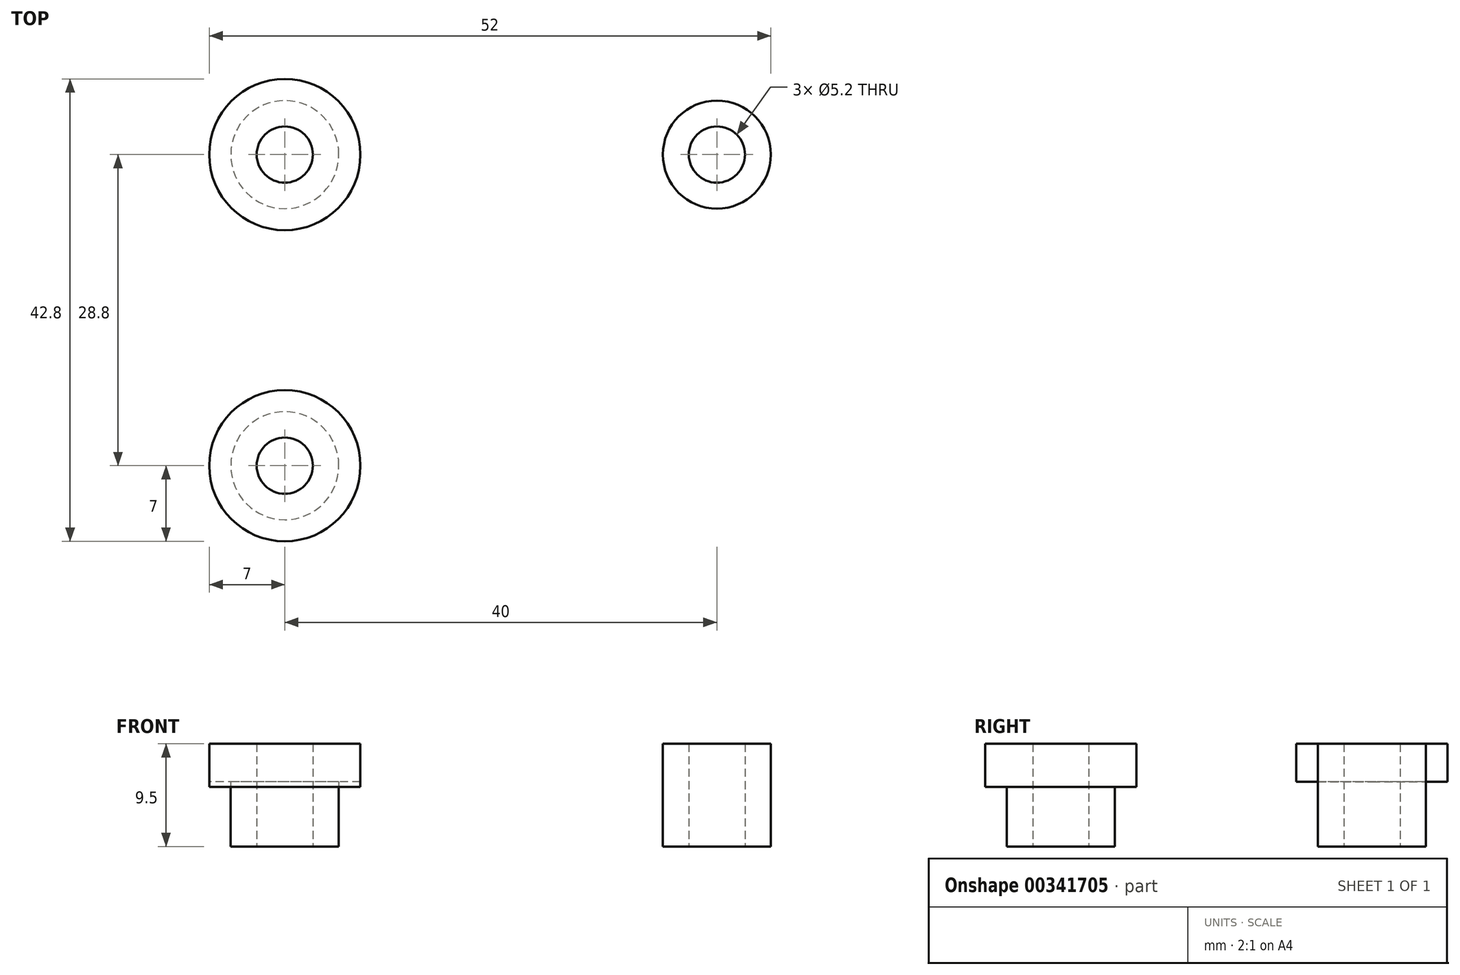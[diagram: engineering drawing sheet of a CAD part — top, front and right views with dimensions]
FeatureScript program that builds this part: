
annotation { "Feature Type Name" : "Feature", "Feature Type Description" : "" }
export const myFeature = defineFeature(function(context is Context, id is Id, definition is map)
    precondition{}
    {
        {
            var Q0;
            Q0=qCreatedBy(makeId("Top.planeOp"),FACE);
            var sketch = newSketch(context, id + "F0", { "sketchPlane" : qUnion([Q0])});
            skCircle(sketch, "E0", {"center": v(0, 0) * mm, "radius": 2.6 * mm});
            skCircle(sketch, "E1", {"center": v(0, 0) * mm, "radius": 5 * mm});
            skSolve(sketch);
        }
        {
            var Q0;
            Q0 = qSketchRegion(id + "F0", true);
            extrude(context, id + "F1", {"entities" : qUnion([Q0]), "depth" : 9.5 * mm});
        }
        {
            var Q0;
            Q0=makeQuery(id+"F1.opExtrude","SWEPT_BODY",BODY,{"disambiguationData":[OSD([sQuery(id+"F0.wireOp",EDGE,"E0"),sQuery(id+"F0.wireOp",EDGE,"E1")])]});
            transform(context, id + "F2", {"entities" : qUnion([Q0]), "transformType" : TransformType.TRANSLATION_3D, "dx" : -40 * mm, "dy" : 0 * mm, "dz" : 0 * mm, "makeCopy" : true});
        }
        {
            var Q0;
            Q0=makeQuery(id+"F2.opPattern","COPY",BODY,{"derivedFrom":makeQuery(id+"F1.opExtrude","SWEPT_BODY",BODY,{"disambiguationData":[OSD([sQuery(id+"F0.wireOp",EDGE,"E0"),sQuery(id+"F0.wireOp",EDGE,"E1")])]}),"instanceName":"1"});
            transform(context, id + "F3", {"entities" : qUnion([Q0]), "transformType" : TransformType.TRANSLATION_3D, "dx" : 0 * mm, "dy" : -28.8 * mm, "dz" : 0 * mm, "makeCopy" : true});
        }
        {
            var Q0;
            Q0=makeQuery(id+"F2.opPattern","COPY",FACE,{"derivedFrom":makeQuery(id+"F1.opExtrude","CAP_FACE",FACE,{"disambiguationData":[OSD([sQuery(id+"F0.wireOp",EDGE,"E0"),sQuery(id+"F0.wireOp",EDGE,"E1")])],"isStart":false}),"instanceName":"1"});
            var sketch = newSketch(context, id + "F4", { "sketchPlane" : qUnion([Q0])});
            skCircle(sketch, "E2", {"center": v(-40, 0) * mm, "radius": 7 * mm});
            skCircle(sketch, "E3", {"center": v(-40, 0) * mm, "radius": 5 * mm});
            skSolve(sketch);
        }
        {
            var Q0;
            Q0=makeQuery(id+"F4.imprint","IMPRINT",FACE,{"disambiguationData":[TD([[makeQuery(id+"F4.imprint","IMPRINT",EDGE,{"derivedFrom":sQuery(id+"F4.wireOp",EDGE,"E2")}),1.0]])]});
            extrude(context, id + "F5", {"entities" : qUnion([Q0]), "operationType" : NewBodyOperationType.ADD, "oppositeDirection" : true, "depth" : 3.5 * mm});
        }
        {
            var Q0;
            Q0=makeQuery(id+"F3.opPattern","COPY",FACE,{"derivedFrom":makeQuery(id+"F2.opPattern","COPY",FACE,{"derivedFrom":makeQuery(id+"F1.opExtrude","CAP_FACE",FACE,{"disambiguationData":[OSD([sQuery(id+"F0.wireOp",EDGE,"E0"),sQuery(id+"F0.wireOp",EDGE,"E1")])],"isStart":false}),"instanceName":"1"}),"instanceName":"1"});
            var sketch = newSketch(context, id + "F6", { "sketchPlane" : qUnion([Q0])});
            skCircle(sketch, "E4", {"center": v(-40, -28.8) * mm, "radius": 5 * mm});
            skCircle(sketch, "E5", {"center": v(-40, -28.8) * mm, "radius": 7 * mm});
            skSolve(sketch);
        }
        {
            var Q0;
            Q0=makeQuery(id+"F6.imprint","IMPRINT",FACE,{"disambiguationData":[TD([[makeQuery(id+"F6.imprint","IMPRINT",EDGE,{"derivedFrom":sQuery(id+"F6.wireOp",EDGE,"E4")}),-1.0]])]});
            extrude(context, id + "F7", {"entities" : qUnion([Q0]), "operationType" : NewBodyOperationType.ADD, "oppositeDirection" : true, "depth" : 4 * mm});
        }
    });
